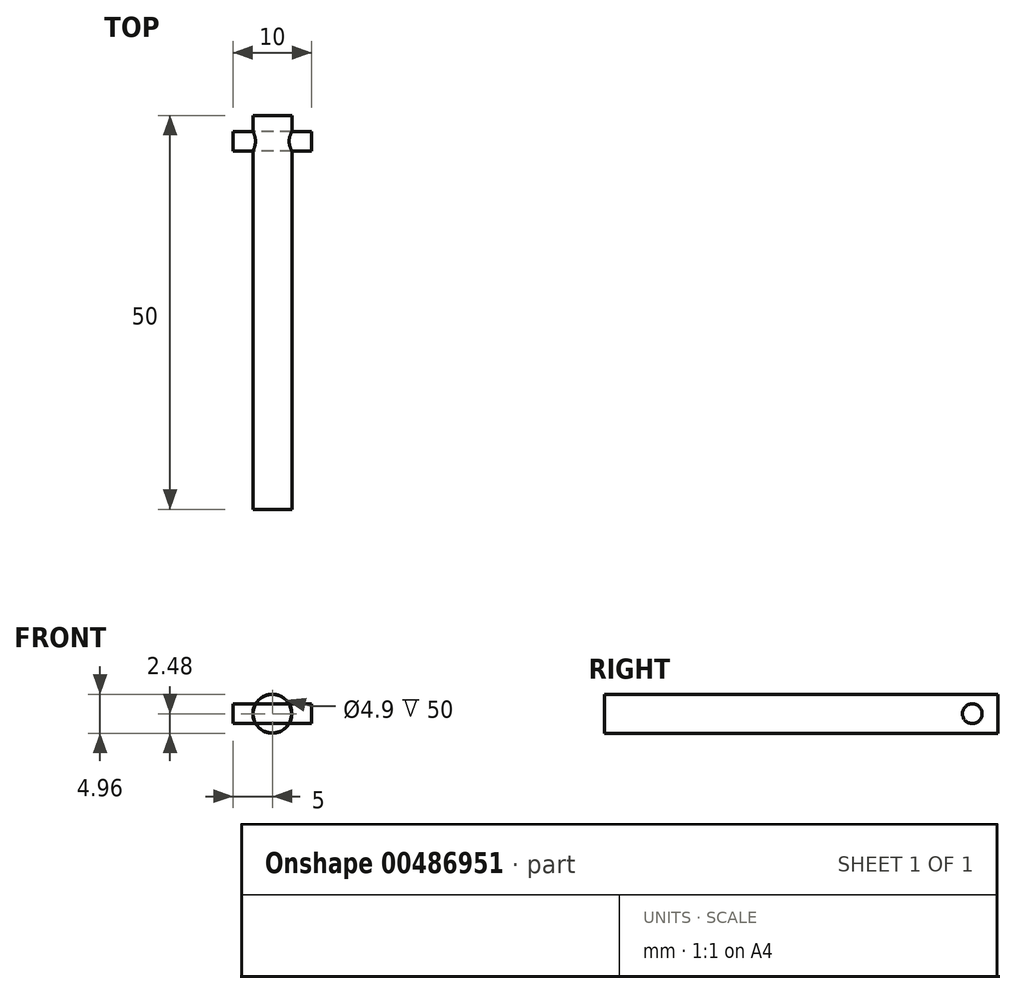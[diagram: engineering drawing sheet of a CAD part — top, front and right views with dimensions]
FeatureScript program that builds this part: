
annotation { "Feature Type Name" : "Feature", "Feature Type Description" : "" }
export const myFeature = defineFeature(function(context is Context, id is Id, definition is map)
    precondition{}
    {
        {
            var Q0;
            Q0=qCreatedBy(makeId("Front.planeOp"),FACE);
            var sketch = newSketch(context, id + "F0", { "sketchPlane" : qUnion([Q0])});
            skCircle(sketch, "E0", {"center": v(0, 0) * mm, "radius": 2.48 * mm});
            skCircle(sketch, "E1", {"center": v(0, 0) * mm, "radius": 2.45 * mm});
            skSolve(sketch);
        }
        {
            var Q0;
            Q0 = qSketchRegion(id + "F0", true);
            extrude(context, id + "F1", {"entities" : qUnion([Q0]), "depth" : 50 * mm});
        }
        {
            var Q0;
            Q0=qCreatedBy(makeId("Right.planeOp"),FACE);
            var sketch = newSketch(context, id + "F2", { "sketchPlane" : qUnion([Q0])});
            skCircle(sketch, "E2", {"center": v(-3.26, 0) * mm, "radius": 1.25 * mm});
            skSolve(sketch);
        }
        {
            var Q0;
            Q0 = qSketchRegion(id + "F2", true);
            extrude(context, id + "F3", {"entities" : qUnion([Q0]), "operationType" : NewBodyOperationType.ADD, "endBound" : BoundingType.SYMMETRIC, "depth" : 10 * mm});
        }
    });
